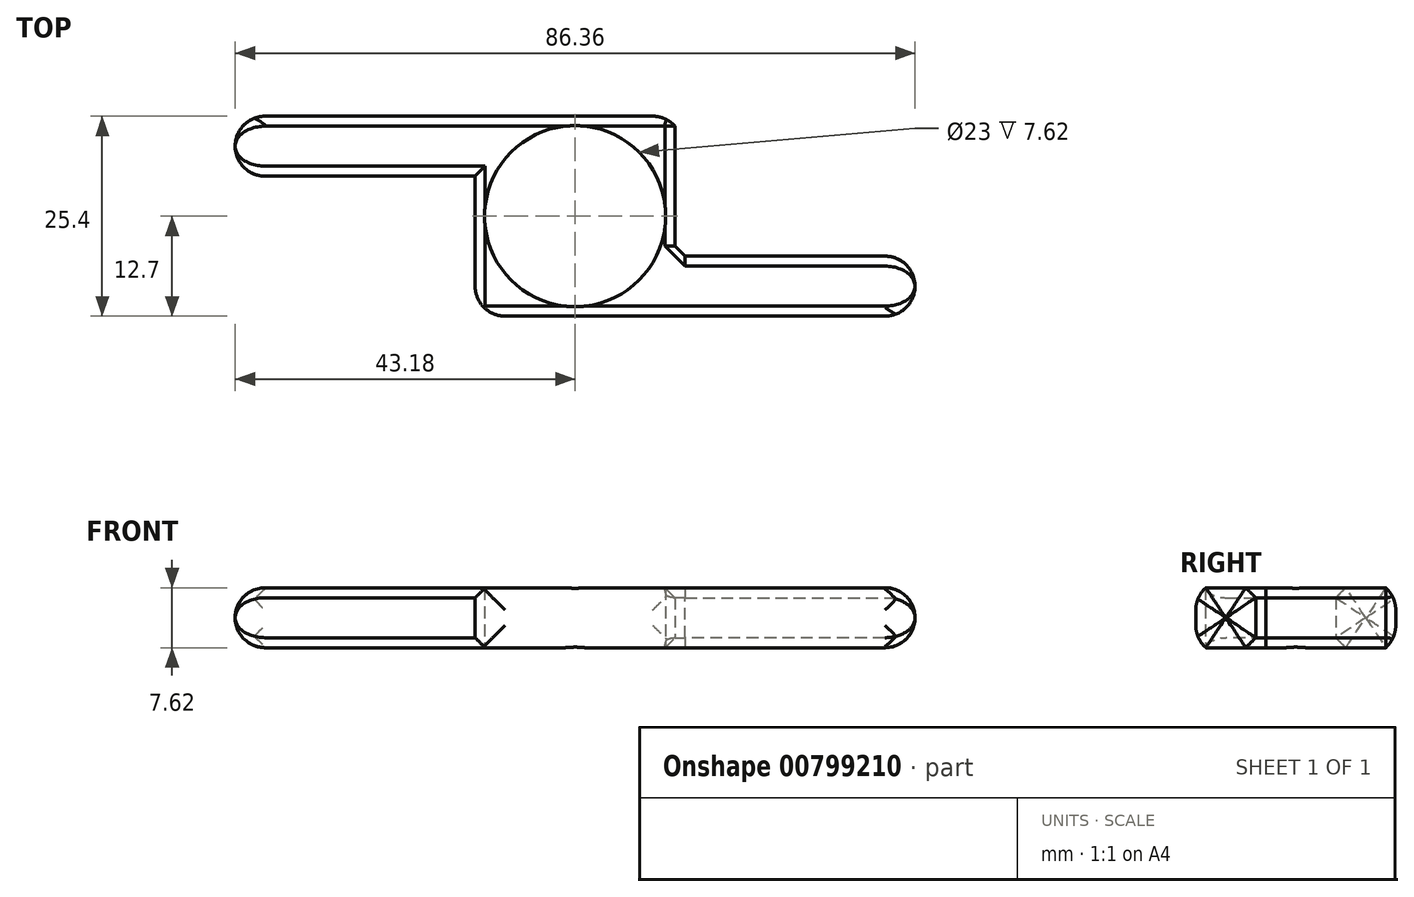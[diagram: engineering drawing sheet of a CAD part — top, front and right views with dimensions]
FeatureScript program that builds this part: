
annotation { "Feature Type Name" : "Feature", "Feature Type Description" : "" }
export const myFeature = defineFeature(function(context is Context, id is Id, definition is map)
    precondition{}
    {
        {
            var Q0;
            Q0=qCreatedBy(makeId("Top.planeOp"),FACE);
            var sketch = newSketch(context, id + "F0", { "sketchPlane" : qUnion([Q0])});
            skCircle(sketch, "E0", {"center": v(0, 0) * mm, "radius": 11.5 * mm});
            skLineSegment(sketch, "E1.bottom", {"start": v(12.7, -12.7) * mm, "end": v(-12.7, -12.7) * mm});
            skLineSegment(sketch, "E1.top", {"start": v(12.7, 12.7) * mm, "end": v(-12.7, 12.7) * mm});
            skLineSegment(sketch, "E1.left", {"start": v(12.7, -12.7) * mm, "end": v(12.7, 12.7) * mm});
            skLineSegment(sketch, "E1.right", {"start": v(-12.7, -12.7) * mm, "end": v(-12.7, 12.7) * mm});
            skLineSegment(sketch, "E2.bottom", {"start": v(-12.7, 12.7) * mm, "end": v(-43.18, 12.7) * mm});
            skLineSegment(sketch, "E2.top", {"start": v(-12.7, 5.08) * mm, "end": v(-43.18, 5.08) * mm});
            skLineSegment(sketch, "E2.left", {"start": v(-12.7, 12.7) * mm, "end": v(-12.7, 5.08) * mm});
            skLineSegment(sketch, "E2.right", {"start": v(-43.18, 12.7) * mm, "end": v(-43.18, 5.08) * mm});
            skLineSegment(sketch, "E3.bottom", {"start": v(12.7, -12.7) * mm, "end": v(43.18, -12.7) * mm});
            skLineSegment(sketch, "E3.top", {"start": v(12.7, -5.08) * mm, "end": v(43.18, -5.08) * mm});
            skLineSegment(sketch, "E3.left", {"start": v(12.7, -12.7) * mm, "end": v(12.7, -5.08) * mm});
            skLineSegment(sketch, "E3.right", {"start": v(43.18, -12.7) * mm, "end": v(43.18, -5.08) * mm});
            skSolve(sketch);
        }
        {
            var Q0;
            {var subQ0=sQuery(id+"F0.wireOp",EDGE,"E2.bottom");Q0=makeQuery(id+"F0.imprint","IMPRINT",FACE,{"disambiguationData":[TD([[makeQuery(id+"F0.imprint","IMPRINT",EDGE,{"derivedFrom":subQ0}),1.0]])]});}
            var Q1;
            Q1=makeQuery(id+"F0.imprint","IMPRINT",FACE,{"disambiguationData":[TD([[makeQuery(id+"F0.imprint","IMPRINT",EDGE,{"derivedFrom":sQuery(id+"F0.wireOp",EDGE,"E0")}),-1.0]])]});
            var Q2;
            {var subQ0=sQuery(id+"F0.wireOp",EDGE,"E3.bottom");Q2=makeQuery(id+"F0.imprint","IMPRINT",FACE,{"disambiguationData":[TD([[makeQuery(id+"F0.imprint","IMPRINT",EDGE,{"derivedFrom":subQ0}),1.0]])]});}
            extrude(context, id + "F1", {"entities" : qUnion([Q0, Q1, Q2]), "depth" : 7.62 * mm, "offsetDistance" : 25.4 * mm});
        }
        {
            var Q0;
            Q0=makeQuery(id+"F1.opExtrude","SWEPT_EDGE",EDGE,{"disambiguationData":[OSD([sQuery(id+"F0.wireOp",EDGE,"E2.top"),sQuery(id+"F0.wireOp",EDGE,"E2.right")])]});
            var Q1;
            Q1=makeQuery(id+"F1.opExtrude","SWEPT_EDGE",EDGE,{"disambiguationData":[OSD([sQuery(id+"F0.wireOp",EDGE,"E2.bottom"),sQuery(id+"F0.wireOp",EDGE,"E2.right")])]});
            var Q2;
            Q2=makeQuery(id+"F1.opExtrude","SWEPT_EDGE",EDGE,{"disambiguationData":[OSD([sQuery(id+"F0.wireOp",EDGE,"E3.bottom"),sQuery(id+"F0.wireOp",EDGE,"E3.right")])]});
            var Q3;
            Q3=makeQuery(id+"F1.opExtrude","SWEPT_EDGE",EDGE,{"disambiguationData":[OSD([sQuery(id+"F0.wireOp",EDGE,"E3.top"),sQuery(id+"F0.wireOp",EDGE,"E3.right")])]});
            var Q4;
            Q4=makeQuery(id+"F1.opExtrude","CAP_EDGE",EDGE,{"disambiguationData":[OSD([sQuery(id+"F0.wireOp",EDGE,"E3.right")])],"isStart":false});
            var Q5;
            Q5=makeQuery(id+"F1.opExtrude","CAP_EDGE",EDGE,{"disambiguationData":[OSD([sQuery(id+"F0.wireOp",EDGE,"E3.right")])],"isStart":true});
            var Q6;
            Q6=makeQuery(id+"F1.opExtrude","CAP_EDGE",EDGE,{"disambiguationData":[OSD([sQuery(id+"F0.wireOp",EDGE,"E2.right")])],"isStart":false});
            var Q7;
            Q7=makeQuery(id+"F1.opExtrude","CAP_EDGE",EDGE,{"disambiguationData":[OSD([sQuery(id+"F0.wireOp",EDGE,"E2.right")])],"isStart":true});
            fillet(context, id + "F2", {"entities" : qUnion([Q0, Q1, Q2, Q3, Q4, Q5, Q6, Q7]), "radius" : 3.8 * mm, "tangentPropagation" : true, "allowEdgeOverflow" : false});
        }
        {
            var Q0;
            Q0=makeQuery(id+"F1.opExtrude","CAP_EDGE",EDGE,{"disambiguationData":[OSD([sQuery(id+"F0.wireOp",EDGE,"E3.top")])],"isStart":true});
            var Q1;
            Q1=makeQuery(id+"F1.opExtrude","CAP_EDGE",EDGE,{"disambiguationData":[OSD([sQuery(id+"F0.wireOp",EDGE,"E2.top")])],"isStart":true});
            var Q2;
            Q2=makeQuery(id+"F1.opExtrude","CAP_EDGE",EDGE,{"disambiguationData":[OSD([sQuery(id+"F0.wireOp",EDGE,"E1.bottom"),sQuery(id+"F0.wireOp",EDGE,"E3.bottom")])],"isStart":true});
            var Q3;
            Q3=makeQuery(id+"F1.opExtrude","CAP_EDGE",EDGE,{"disambiguationData":[OSD([sQuery(id+"F0.wireOp",EDGE,"E1.top"),sQuery(id+"F0.wireOp",EDGE,"E2.bottom")])],"isStart":true});
            var Q4;
            Q4=makeQuery(id+"F1.opExtrude","CAP_EDGE",EDGE,{"disambiguationData":[OSD([sQuery(id+"F0.wireOp",EDGE,"E1.bottom"),sQuery(id+"F0.wireOp",EDGE,"E3.bottom")])],"isStart":false});
            var Q5;
            Q5=makeQuery(id+"F1.opExtrude","CAP_EDGE",EDGE,{"disambiguationData":[OSD([sQuery(id+"F0.wireOp",EDGE,"E3.top")])],"isStart":false});
            var Q6;
            Q6=makeQuery(id+"F1.opExtrude","CAP_EDGE",EDGE,{"disambiguationData":[OSD([sQuery(id+"F0.wireOp",EDGE,"E1.top"),sQuery(id+"F0.wireOp",EDGE,"E2.bottom")])],"isStart":false});
            var Q7;
            Q7=makeQuery(id+"F1.opExtrude","CAP_EDGE",EDGE,{"disambiguationData":[OSD([sQuery(id+"F0.wireOp",EDGE,"E2.top")])],"isStart":false});
            var Q8;
            Q8=makeQuery(id+"F1.opExtrude","SWEPT_FACE",FACE,{"disambiguationData":[OSD([sQuery(id+"F0.wireOp",EDGE,"E1.left")])]});
            var Q9;
            Q9=makeQuery(id+"F1.opExtrude","CAP_EDGE",EDGE,{"disambiguationData":[OSD([sQuery(id+"F0.wireOp",EDGE,"E1.right")])],"isStart":true});
            var Q10;
            Q10=makeQuery(id+"F1.opExtrude","CAP_EDGE",EDGE,{"disambiguationData":[OSD([sQuery(id+"F0.wireOp",EDGE,"E1.right")])],"isStart":false});
            chamfer(context, id + "F3", {"entities" : qUnion([Q0, Q1, Q2, Q3, Q4, Q5, Q6, Q7, Q8, Q9, Q10]), "width" : 1.27 * mm, "tangentPropagation" : true});
        }
        {
            var Q0;
            Q0=makeQuery(id+"F1.opExtrude","SWEPT_FACE",FACE,{"disambiguationData":[OSD([sQuery(id+"F0.wireOp",EDGE,"E1.bottom"),sQuery(id+"F0.wireOp",EDGE,"E3.bottom")])]});
            var Q1;
            Q1=makeQuery(id+"F1.opExtrude","SWEPT_FACE",FACE,{"disambiguationData":[OSD([sQuery(id+"F0.wireOp",EDGE,"E1.top"),sQuery(id+"F0.wireOp",EDGE,"E2.bottom")])]});
            fillet(context, id + "F4", {"entities" : qUnion([Q0, Q1]), "radius" : 3.8 * mm, "tangentPropagation" : true, "allowEdgeOverflow" : false});
        }
    });
